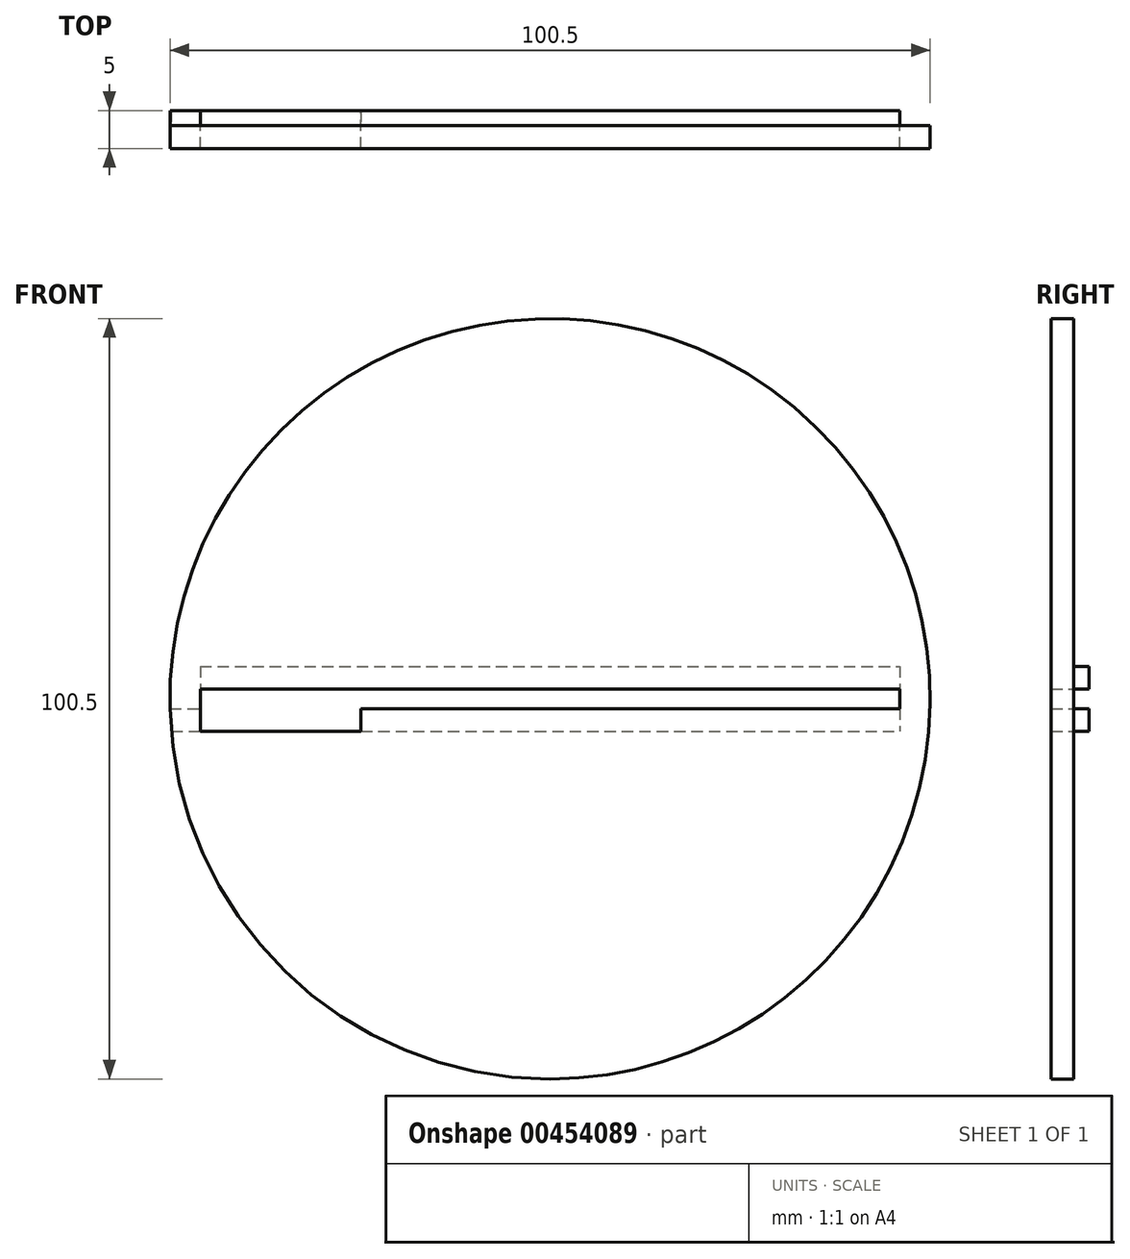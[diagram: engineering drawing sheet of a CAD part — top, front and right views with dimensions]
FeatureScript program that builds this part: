
annotation { "Feature Type Name" : "Feature", "Feature Type Description" : "" }
export const myFeature = defineFeature(function(context is Context, id is Id, definition is map)
    precondition{}
    {
        {
            var Q0;
            Q0=qCreatedBy(makeId("Front.planeOp"),FACE);
            var sketch = newSketch(context, id + "F0", { "sketchPlane" : qUnion([Q0])});
            skCircle(sketch, "E0", {"center": v(0, 0) * mm, "radius": 50.25 * mm});
            skLineSegment(sketch, "E1", {"start": v(-50.23, 1.3) * mm, "end": v(50.23, 1.3) * mm});
            skLineSegment(sketch, "E2", {"start": v(-50.07, 4.3) * mm, "end": v(50.07, 4.3) * mm});
            skLineSegment(sketch, "E3.MirrorCS", {"start": v(-50.23, -1.3) * mm, "end": v(50.23, -1.3) * mm});
            skLineSegment(sketch, "E4.MirrorCS", {"start": v(-50.07, -4.3) * mm, "end": v(50.07, -4.3) * mm});
            skLineSegment(sketch, "E5", {"start": v(-25, 4.3) * mm, "end": v(-25, -4.3) * mm});
            skLineSegment(sketch, "E6.MirrorCS", {"start": v(25, 4.3) * mm, "end": v(25, -4.3) * mm});
            skLineSegment(sketch, "E7", {"start": v(-46.25, 1.3) * mm, "end": v(-46.25, -1.3) * mm});
            skLineSegment(sketch, "E8", {"start": v(46.25, 1.3) * mm, "end": v(46.25, -1.3) * mm});
            skLineSegment(sketch, "E9", {"start": v(-46.25, -1.3) * mm, "end": v(-46.25, -4.3) * mm});
            skLineSegment(sketch, "E10", {"start": v(-46.25, -4.3) * mm, "end": v(-46.25, 1.3) * mm});
            skLineSegment(sketch, "E11", {"start": v(-46.25, 4.3) * mm, "end": v(-46.25, 1.3) * mm});
            skLineSegment(sketch, "E12", {"start": v(46.25, -1.3) * mm, "end": v(46.25, -4.3) * mm});
            skLineSegment(sketch, "E13", {"start": v(46.25, -4.3) * mm, "end": v(46.25, 1.3) * mm});
            skLineSegment(sketch, "E14", {"start": v(46.25, 4.3) * mm, "end": v(46.25, 1.3) * mm});
            skPoint(sketch, "E15", {"position": v(-46.75, 0) * mm});
            skPoint(sketch, "E16", {"position": v(46.75, 0) * mm});
            skSolve(sketch);
        }
        {
            var Q0;
            Q0 = qSketchRegion(id + "F0", true);
            var Q1;
            {var subQ0=sQuery(id+"F0.wireOp",EDGE,"E5");var subQ1=sQuery(id+"F0.wireOp",EDGE,"E3.MirrorCS");var subQ2=makeQuery(id+"F0.imprint","INTERSECT",VERTEX,{"derivedFrom":[subQ1,subQ0]});Q1=makeQuery(id+"F0.imprint","IMPRINT",FACE,{"disambiguationData":[TD([[makeQuery(id+"F0.imprint","IMPRINT",EDGE,{"disambiguationData":[TD([[subQ2,-1.0]])],"derivedFrom":subQ1}),-1.0]])]});}
            var Q2;
            {var subQ0=sQuery(id+"F0.wireOp",EDGE,"E5");var subQ1=sQuery(id+"F0.wireOp",EDGE,"E1");var subQ2=makeQuery(id+"F0.imprint","INTERSECT",VERTEX,{"derivedFrom":[subQ1,subQ0]});Q2=makeQuery(id+"F0.imprint","IMPRINT",FACE,{"disambiguationData":[TD([[makeQuery(id+"F0.imprint","IMPRINT",EDGE,{"disambiguationData":[TD([[subQ2,-1.0]])],"derivedFrom":subQ1}),1.0]])]});}
            var Q3;
            {var subQ0=sQuery(id+"F0.wireOp",EDGE,"E11");Q3=makeQuery(id+"F0.imprint","IMPRINT",FACE,{"disambiguationData":[TD([[makeQuery(id+"F0.imprint","IMPRINT",EDGE,{"derivedFrom":subQ0}),1.0]])]});}
            var Q4;
            {var subQ0=sQuery(id+"F0.wireOp",EDGE,"E14");Q4=makeQuery(id+"F0.imprint","IMPRINT",FACE,{"disambiguationData":[TD([[makeQuery(id+"F0.imprint","IMPRINT",EDGE,{"derivedFrom":subQ0}),-1.0]])]});}
            var Q5;
            {var subQ0=sQuery(id+"F0.wireOp",EDGE,"E6.MirrorCS");var subQ1=sQuery(id+"F0.wireOp",EDGE,"E3.MirrorCS");var subQ2=makeQuery(id+"F0.imprint","INTERSECT",VERTEX,{"derivedFrom":[subQ1,subQ0]});Q5=makeQuery(id+"F0.imprint","IMPRINT",FACE,{"disambiguationData":[TD([[makeQuery(id+"F0.imprint","IMPRINT",EDGE,{"disambiguationData":[TD([[subQ2,-1.0]])],"derivedFrom":subQ1}),-1.0]])]});}
            var Q6;
            {var subQ0=sQuery(id+"F0.wireOp",EDGE,"E10");var subQ1=sQuery(id+"F0.wireOp",EDGE,"E3.MirrorCS");var subQ2=makeQuery(id+"F0.imprint","INTERSECT",VERTEX,{"derivedFrom":[subQ1,subQ0]});Q6=makeQuery(id+"F0.imprint","IMPRINT",FACE,{"disambiguationData":[TD([[makeQuery(id+"F0.imprint","IMPRINT",EDGE,{"disambiguationData":[TD([[subQ2,-1.0]])],"derivedFrom":subQ1}),-1.0]])]});}
            extrude(context, id + "F1", {"entities" : qUnion([Q0, Q1, Q2, Q3, Q4, Q5, Q6]), "depth" : 3 * mm});
        }
        {
            var Q0;
            {var subQ0=sQuery(id+"F0.wireOp",EDGE,"E5");var subQ1=sQuery(id+"F0.wireOp",EDGE,"E3.MirrorCS");var subQ2=makeQuery(id+"F0.imprint","INTERSECT",VERTEX,{"derivedFrom":[subQ1,subQ0]});Q0=makeQuery(id+"F0.imprint","IMPRINT",FACE,{"disambiguationData":[TD([[makeQuery(id+"F0.imprint","IMPRINT",EDGE,{"disambiguationData":[TD([[subQ2,-1.0]])],"derivedFrom":subQ1}),-1.0]])]});}
            var Q1;
            {var subQ0=sQuery(id+"F0.wireOp",EDGE,"E5");var subQ1=sQuery(id+"F0.wireOp",EDGE,"E1");var subQ2=makeQuery(id+"F0.imprint","INTERSECT",VERTEX,{"derivedFrom":[subQ1,subQ0]});Q1=makeQuery(id+"F0.imprint","IMPRINT",FACE,{"disambiguationData":[TD([[makeQuery(id+"F0.imprint","IMPRINT",EDGE,{"disambiguationData":[TD([[subQ2,-1.0]])],"derivedFrom":subQ1}),1.0]])]});}
            var Q2;
            {var subQ0=sQuery(id+"F0.wireOp",EDGE,"E6.MirrorCS");var subQ1=sQuery(id+"F0.wireOp",EDGE,"E3.MirrorCS");var subQ2=makeQuery(id+"F0.imprint","INTERSECT",VERTEX,{"derivedFrom":[subQ1,subQ0]});Q2=makeQuery(id+"F0.imprint","IMPRINT",FACE,{"disambiguationData":[TD([[makeQuery(id+"F0.imprint","IMPRINT",EDGE,{"disambiguationData":[TD([[subQ2,-1.0]])],"derivedFrom":subQ1}),-1.0]])]});}
            var Q3;
            {var subQ0=sQuery(id+"F0.wireOp",EDGE,"E14");Q3=makeQuery(id+"F0.imprint","IMPRINT",FACE,{"disambiguationData":[TD([[makeQuery(id+"F0.imprint","IMPRINT",EDGE,{"derivedFrom":subQ0}),-1.0]])]});}
            var Q4;
            {var subQ0=sQuery(id+"F0.wireOp",EDGE,"E11");Q4=makeQuery(id+"F0.imprint","IMPRINT",FACE,{"disambiguationData":[TD([[makeQuery(id+"F0.imprint","IMPRINT",EDGE,{"derivedFrom":subQ0}),1.0]])]});}
            var Q5;
            {var subQ0=sQuery(id+"F0.wireOp",EDGE,"E10");var subQ1=sQuery(id+"F0.wireOp",EDGE,"E3.MirrorCS");var subQ2=makeQuery(id+"F0.imprint","INTERSECT",VERTEX,{"derivedFrom":[subQ1,subQ0]});Q5=makeQuery(id+"F0.imprint","IMPRINT",FACE,{"disambiguationData":[TD([[makeQuery(id+"F0.imprint","IMPRINT",EDGE,{"disambiguationData":[TD([[subQ2,-1.0]])],"derivedFrom":subQ1}),-1.0]])]});}
            extrude(context, id + "F2", {"entities" : qUnion([Q0, Q1, Q2, Q3, Q4, Q5]), "operationType" : NewBodyOperationType.ADD, "oppositeDirection" : true, "depth" : 2 * mm});
        }
    });
